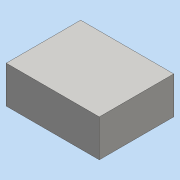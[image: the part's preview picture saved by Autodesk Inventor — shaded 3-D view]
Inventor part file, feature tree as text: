
AUTODESK INVENTOR PART (.ipt)
format: ipt  version: 2016 (Build 200138000, 138)  size: 69,120 bytes
history: native  units: mm
features: extrude x1, sketch x1
ambient origin geometry x8: Origin, YZ Plane, XZ Plane, XY Plane, X Axis, Y Axis, Z Axis, Center Point
bodies: Solid1 (feature_tree)
feature tree (2):
  extrude  "Extrusion1"  Depth=127.0mm
  sketch  "Sketch1"  dims[d0=50.8mm d1=127.0mm d2=101.6mm d3=0.0mm]
